# Revit family: Graypants_Scraplights_Frame_Dome36_R21_0925
name_source: partatom
category: Lighting Fixtures
units: mm (PartAtom-declared; Revit-internal decimal feet)

## family parameters
Cut with Voids When Loaded = No
Host = Face
Light Source = Yes
Part Type = Normal
Room Calculation Point = No
Round Connector Dimension = Use Diameter
Shared = No

## types (1)
- Graypants_Scraplights_Dome36_Pendant
    Color Filter = 16777215
    Default Elevation = 4' - 0"
    Dimming Lamp Color Temperature Shift = <None>
    Graypants_Canopy_Visible = Yes
    Graypants_Cord/Canopy_Finish_Options = White | Black
    Graypants_Cord_Visible = Yes
    Graypants_Manufacturer = Graypants
    Graypants_Model = Scraplights_Frame_Dome_36
    Graypants_Shade_Finish_Options = Natural Cardboard | Blonde Cardboard | White Cardboard
    Graypants_Shade_Visible = Yes
    Light Source Symbol Size = 3' - 0 3/8"

## geometry (parser evidence)
native form markers: Sweep x9
no freeform markers — native parametric forms only
